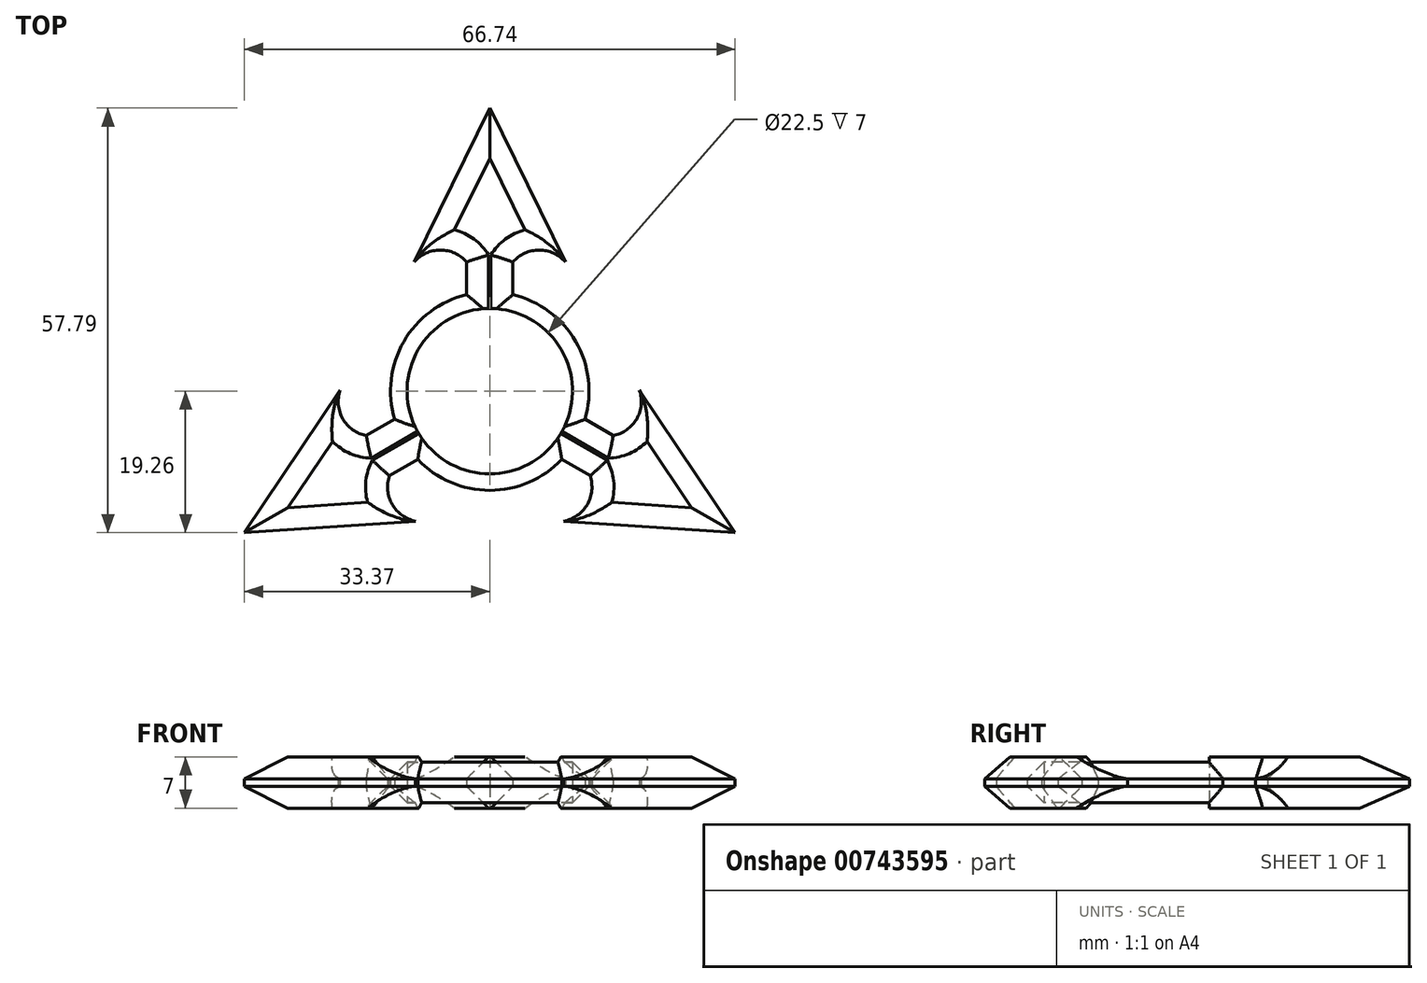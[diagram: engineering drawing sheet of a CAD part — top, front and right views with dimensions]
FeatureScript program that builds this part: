
annotation { "Feature Type Name" : "Feature", "Feature Type Description" : "" }
export const myFeature = defineFeature(function(context is Context, id is Id, definition is map)
    precondition{}
    {
        {
            var Q0;
            Q0=qCreatedBy(makeId("Top.planeOp"),FACE);
            var sketch = newSketch(context, id + "F0", { "sketchPlane" : qUnion([Q0])});
            skCircle(sketch, "E0", {"center": v(0, 0) * mm, "radius": 11.25 * mm});
            skCircle(sketch, "E1", {"center": v(0, 0) * mm, "radius": 13.5 * mm});
            skLineSegment(sketch, "E2", {"start": v(-3.15, 13.13) * mm, "end": v(-3.15, 17.57) * mm});
            skArc(sketch, "E3", {"start": v(-3.15, 17.57) * mm, "mid": v(-6.72, 19.2) * mm, "end": v(-10.28, 17.57) * mm});
            skLineSegment(sketch, "E4", {"start": v(-10.28, 17.57) * mm, "end": v(0, 38.53) * mm});
            skLineSegment(sketch, "E5.MirrorCS", {"start": v(10.28, 17.57) * mm, "end": v(0, 38.53) * mm});
            skArc(sketch, "E6.MirrorCS", {"start": v(3.15, 17.57) * mm, "mid": v(6.72, 19.2) * mm, "end": v(10.28, 17.57) * mm});
            skLineSegment(sketch, "E7.MirrorCS", {"start": v(3.15, 13.13) * mm, "end": v(3.15, 17.57) * mm});
            skLineSegment(sketch, "E8.1.0", {"start": v(-10.07, -17.69) * mm, "end": v(-33.37, -19.26) * mm});
            skArc(sketch, "E8.1.1", {"start": v(-13.64, -11.51) * mm, "mid": v(-13.27, -15.42) * mm, "end": v(-10.07, -17.69) * mm});
            skLineSegment(sketch, "E8.1.2", {"start": v(-9.8, -9.3) * mm, "end": v(-13.64, -11.51) * mm});
            skLineSegment(sketch, "E8.1.3", {"start": v(-12.94, -3.83) * mm, "end": v(-16.8, -6.05) * mm});
            skArc(sketch, "E8.1.4", {"start": v(-16.8, -6.05) * mm, "mid": v(-19.98, -3.78) * mm, "end": v(-20.35, 0.12) * mm});
            skLineSegment(sketch, "E8.1.5", {"start": v(-20.35, 0.12) * mm, "end": v(-33.37, -19.26) * mm});
            skLineSegment(sketch, "E8.2.0", {"start": v(20.35, 0.12) * mm, "end": v(33.37, -19.26) * mm});
            skArc(sketch, "E8.2.1", {"start": v(16.8, -6.05) * mm, "mid": v(19.98, -3.78) * mm, "end": v(20.35, 0.12) * mm});
            skLineSegment(sketch, "E8.2.2", {"start": v(12.94, -3.83) * mm, "end": v(16.8, -6.05) * mm});
            skLineSegment(sketch, "E8.2.3", {"start": v(9.8, -9.3) * mm, "end": v(13.64, -11.51) * mm});
            skArc(sketch, "E8.2.4", {"start": v(13.64, -11.51) * mm, "mid": v(13.27, -15.42) * mm, "end": v(10.07, -17.69) * mm});
            skLineSegment(sketch, "E8.2.5", {"start": v(10.07, -17.69) * mm, "end": v(33.37, -19.26) * mm});
            skSolve(sketch);
        }
        {
            var Q0;
            Q0 = qSketchRegion(id + "F0", true);
            extrude(context, id + "F1", {"entities" : qUnion([Q0]), "depth" : 7 * mm, "offsetDistance" : 25 * mm});
        }
        {
            var Q0;
            Q0=makeQuery(id+"F1.opExtrude","CAP_EDGE",EDGE,{"disambiguationData":[OSD([sQuery(id+"F0.wireOp",EDGE,"E4")])],"isStart":false});
            var Q1;
            Q1=makeQuery(id+"F1.opExtrude","CAP_EDGE",EDGE,{"disambiguationData":[OSD([sQuery(id+"F0.wireOp",EDGE,"E3")])],"isStart":false});
            var Q2;
            Q2=makeQuery(id+"F1.opExtrude","CAP_EDGE",EDGE,{"disambiguationData":[OSD([sQuery(id+"F0.wireOp",EDGE,"E2")])],"isStart":false});
            var Q3;
            {var subQ0=sQuery(id+"F0.wireOp",EDGE,"E1");Q3=makeQuery(id+"F1.opExtrude","CAP_EDGE",EDGE,{"disambiguationData":[OSD([subQ0]),TDD([makeQuery(id+"F0.imprint","IMPRINT",EDGE,{"disambiguationData":[TD([[makeQuery(id+"F0.imprint","INTERSECT",VERTEX,{"derivedFrom":[subQ0,sQuery(id+"F0.wireOp",EDGE,"E2")]}),-1.0]])],"derivedFrom":subQ0})])],"isStart":false});}
            var Q4;
            Q4=makeQuery(id+"F1.opExtrude","CAP_EDGE",EDGE,{"disambiguationData":[OSD([sQuery(id+"F0.wireOp",EDGE,"E8.1.3")])],"isStart":false});
            var Q5;
            Q5=makeQuery(id+"F1.opExtrude","CAP_EDGE",EDGE,{"disambiguationData":[OSD([sQuery(id+"F0.wireOp",EDGE,"E8.1.4")])],"isStart":false});
            var Q6;
            Q6=makeQuery(id+"F1.opExtrude","CAP_EDGE",EDGE,{"disambiguationData":[OSD([sQuery(id+"F0.wireOp",EDGE,"E8.1.5")])],"isStart":false});
            var Q7;
            Q7=makeQuery(id+"F1.opExtrude","CAP_EDGE",EDGE,{"disambiguationData":[OSD([sQuery(id+"F0.wireOp",EDGE,"E8.1.0")])],"isStart":false});
            var Q8;
            Q8=makeQuery(id+"F1.opExtrude","CAP_EDGE",EDGE,{"disambiguationData":[OSD([sQuery(id+"F0.wireOp",EDGE,"E8.1.1")])],"isStart":false});
            var Q9;
            Q9=makeQuery(id+"F1.opExtrude","CAP_EDGE",EDGE,{"disambiguationData":[OSD([sQuery(id+"F0.wireOp",EDGE,"E8.1.2")])],"isStart":false});
            var Q10;
            {var subQ0=sQuery(id+"F0.wireOp",EDGE,"E1");Q10=makeQuery(id+"F1.opExtrude","CAP_EDGE",EDGE,{"disambiguationData":[OSD([subQ0]),TDD([makeQuery(id+"F0.imprint","IMPRINT",EDGE,{"disambiguationData":[TD([[makeQuery(id+"F0.imprint","INTERSECT",VERTEX,{"derivedFrom":[subQ0,sQuery(id+"F0.wireOp",EDGE,"E8.1.2")]}),-1.0]])],"derivedFrom":subQ0})])],"isStart":false});}
            var Q11;
            Q11=makeQuery(id+"F1.opExtrude","CAP_EDGE",EDGE,{"disambiguationData":[OSD([sQuery(id+"F0.wireOp",EDGE,"E8.2.3")])],"isStart":false});
            var Q12;
            Q12=makeQuery(id+"F1.opExtrude","CAP_EDGE",EDGE,{"disambiguationData":[OSD([sQuery(id+"F0.wireOp",EDGE,"E8.2.4")])],"isStart":false});
            var Q13;
            Q13=makeQuery(id+"F1.opExtrude","CAP_EDGE",EDGE,{"disambiguationData":[OSD([sQuery(id+"F0.wireOp",EDGE,"E8.2.5")])],"isStart":false});
            var Q14;
            Q14=makeQuery(id+"F1.opExtrude","CAP_EDGE",EDGE,{"disambiguationData":[OSD([sQuery(id+"F0.wireOp",EDGE,"E8.2.0")])],"isStart":false});
            var Q15;
            Q15=makeQuery(id+"F1.opExtrude","CAP_EDGE",EDGE,{"disambiguationData":[OSD([sQuery(id+"F0.wireOp",EDGE,"E8.2.1")])],"isStart":false});
            var Q16;
            Q16=makeQuery(id+"F1.opExtrude","CAP_EDGE",EDGE,{"disambiguationData":[OSD([sQuery(id+"F0.wireOp",EDGE,"E8.2.2")])],"isStart":false});
            var Q17;
            {var subQ0=sQuery(id+"F0.wireOp",EDGE,"E1");Q17=makeQuery(id+"F1.opExtrude","CAP_EDGE",EDGE,{"disambiguationData":[OSD([subQ0]),TDD([makeQuery(id+"F0.imprint","IMPRINT",EDGE,{"disambiguationData":[TD([[makeQuery(id+"F0.imprint","INTERSECT",VERTEX,{"derivedFrom":[subQ0,sQuery(id+"F0.wireOp",EDGE,"E7.MirrorCS")]}),1.0]])],"derivedFrom":subQ0})])],"isStart":false});}
            var Q18;
            Q18=makeQuery(id+"F1.opExtrude","CAP_EDGE",EDGE,{"disambiguationData":[OSD([sQuery(id+"F0.wireOp",EDGE,"E7.MirrorCS")])],"isStart":false});
            var Q19;
            Q19=makeQuery(id+"F1.opExtrude","CAP_EDGE",EDGE,{"disambiguationData":[OSD([sQuery(id+"F0.wireOp",EDGE,"E6.MirrorCS")])],"isStart":false});
            var Q20;
            Q20=makeQuery(id+"F1.opExtrude","CAP_EDGE",EDGE,{"disambiguationData":[OSD([sQuery(id+"F0.wireOp",EDGE,"E5.MirrorCS")])],"isStart":false});
            var Q21;
            Q21=makeQuery(id+"F1.opExtrude","CAP_EDGE",EDGE,{"disambiguationData":[OSD([sQuery(id+"F0.wireOp",EDGE,"E3")])],"isStart":true});
            var Q22;
            Q22=makeQuery(id+"F1.opExtrude","CAP_EDGE",EDGE,{"disambiguationData":[OSD([sQuery(id+"F0.wireOp",EDGE,"E4")])],"isStart":true});
            var Q23;
            Q23=makeQuery(id+"F1.opExtrude","CAP_EDGE",EDGE,{"disambiguationData":[OSD([sQuery(id+"F0.wireOp",EDGE,"E5.MirrorCS")])],"isStart":true});
            var Q24;
            Q24=makeQuery(id+"F1.opExtrude","CAP_EDGE",EDGE,{"disambiguationData":[OSD([sQuery(id+"F0.wireOp",EDGE,"E6.MirrorCS")])],"isStart":true});
            var Q25;
            Q25=makeQuery(id+"F1.opExtrude","CAP_EDGE",EDGE,{"disambiguationData":[OSD([sQuery(id+"F0.wireOp",EDGE,"E7.MirrorCS")])],"isStart":true});
            var Q26;
            {var subQ0=sQuery(id+"F0.wireOp",EDGE,"E1");Q26=makeQuery(id+"F1.opExtrude","CAP_EDGE",EDGE,{"disambiguationData":[OSD([subQ0]),TDD([makeQuery(id+"F0.imprint","IMPRINT",EDGE,{"disambiguationData":[TD([[makeQuery(id+"F0.imprint","INTERSECT",VERTEX,{"derivedFrom":[subQ0,sQuery(id+"F0.wireOp",EDGE,"E7.MirrorCS")]}),1.0]])],"derivedFrom":subQ0})])],"isStart":true});}
            var Q27;
            Q27=makeQuery(id+"F1.opExtrude","CAP_EDGE",EDGE,{"disambiguationData":[OSD([sQuery(id+"F0.wireOp",EDGE,"E8.2.2")])],"isStart":true});
            var Q28;
            Q28=makeQuery(id+"F1.opExtrude","CAP_EDGE",EDGE,{"disambiguationData":[OSD([sQuery(id+"F0.wireOp",EDGE,"E8.2.1")])],"isStart":true});
            var Q29;
            Q29=makeQuery(id+"F1.opExtrude","CAP_EDGE",EDGE,{"disambiguationData":[OSD([sQuery(id+"F0.wireOp",EDGE,"E8.2.0")])],"isStart":true});
            var Q30;
            Q30=makeQuery(id+"F1.opExtrude","CAP_EDGE",EDGE,{"disambiguationData":[OSD([sQuery(id+"F0.wireOp",EDGE,"E8.2.5")])],"isStart":true});
            var Q31;
            Q31=makeQuery(id+"F1.opExtrude","CAP_EDGE",EDGE,{"disambiguationData":[OSD([sQuery(id+"F0.wireOp",EDGE,"E8.2.4")])],"isStart":true});
            var Q32;
            Q32=makeQuery(id+"F1.opExtrude","CAP_EDGE",EDGE,{"disambiguationData":[OSD([sQuery(id+"F0.wireOp",EDGE,"E8.2.3")])],"isStart":true});
            var Q33;
            {var subQ0=sQuery(id+"F0.wireOp",EDGE,"E1");Q33=makeQuery(id+"F1.opExtrude","CAP_EDGE",EDGE,{"disambiguationData":[OSD([subQ0]),TDD([makeQuery(id+"F0.imprint","IMPRINT",EDGE,{"disambiguationData":[TD([[makeQuery(id+"F0.imprint","INTERSECT",VERTEX,{"derivedFrom":[subQ0,sQuery(id+"F0.wireOp",EDGE,"E8.1.2")]}),-1.0]])],"derivedFrom":subQ0})])],"isStart":true});}
            var Q34;
            Q34=makeQuery(id+"F1.opExtrude","CAP_EDGE",EDGE,{"disambiguationData":[OSD([sQuery(id+"F0.wireOp",EDGE,"E8.1.2")])],"isStart":true});
            var Q35;
            Q35=makeQuery(id+"F1.opExtrude","CAP_EDGE",EDGE,{"disambiguationData":[OSD([sQuery(id+"F0.wireOp",EDGE,"E8.1.1")])],"isStart":true});
            var Q36;
            Q36=makeQuery(id+"F1.opExtrude","CAP_EDGE",EDGE,{"disambiguationData":[OSD([sQuery(id+"F0.wireOp",EDGE,"E8.1.0")])],"isStart":true});
            var Q37;
            Q37=makeQuery(id+"F1.opExtrude","CAP_EDGE",EDGE,{"disambiguationData":[OSD([sQuery(id+"F0.wireOp",EDGE,"E8.1.5")])],"isStart":true});
            var Q38;
            Q38=makeQuery(id+"F1.opExtrude","CAP_EDGE",EDGE,{"disambiguationData":[OSD([sQuery(id+"F0.wireOp",EDGE,"E8.1.4")])],"isStart":true});
            var Q39;
            Q39=makeQuery(id+"F1.opExtrude","CAP_EDGE",EDGE,{"disambiguationData":[OSD([sQuery(id+"F0.wireOp",EDGE,"E8.1.3")])],"isStart":true});
            var Q40;
            {var subQ0=sQuery(id+"F0.wireOp",EDGE,"E1");Q40=makeQuery(id+"F1.opExtrude","CAP_EDGE",EDGE,{"disambiguationData":[OSD([subQ0]),TDD([makeQuery(id+"F0.imprint","IMPRINT",EDGE,{"disambiguationData":[TD([[makeQuery(id+"F0.imprint","INTERSECT",VERTEX,{"derivedFrom":[subQ0,sQuery(id+"F0.wireOp",EDGE,"E2")]}),-1.0]])],"derivedFrom":subQ0})])],"isStart":true});}
            var Q41;
            Q41=makeQuery(id+"F1.opExtrude","CAP_EDGE",EDGE,{"disambiguationData":[OSD([sQuery(id+"F0.wireOp",EDGE,"E2")])],"isStart":true});
            chamfer(context, id + "F2", {"entities" : qUnion([Q0, Q1, Q2, Q3, Q4, Q5, Q6, Q7, Q8, Q9, Q10, Q11, Q12, Q13, Q14, Q15, Q16, Q17, Q18, Q19, Q20, Q21, Q22, Q23, Q24, Q25, Q26, Q27, Q28, Q29, Q30, Q31, Q32, Q33, Q34, Q35, Q36, Q37, Q38, Q39, Q40, Q41]), "width" : 3 * mm, "tangentPropagation" : true});
        }
    });
